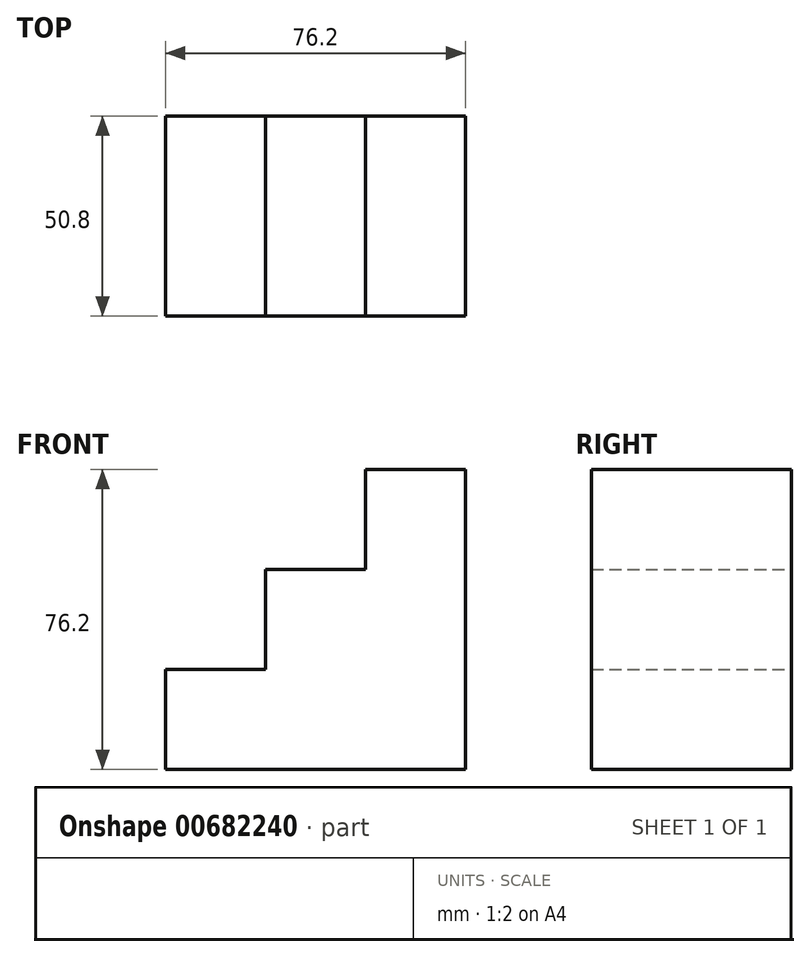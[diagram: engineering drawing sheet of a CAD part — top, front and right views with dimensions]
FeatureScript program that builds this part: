
annotation { "Feature Type Name" : "Feature", "Feature Type Description" : "" }
export const myFeature = defineFeature(function(context is Context, id is Id, definition is map)
    precondition{}
    {
        {
            var Q0;
            Q0=qCreatedBy(makeId("Front.planeOp"),FACE);
            var sketch = newSketch(context, id + "F0", { "sketchPlane" : qUnion([Q0])});
            skLineSegment(sketch, "E0", {"start": v(-41.97, -41.18) * mm, "end": v(34.23, -41.18) * mm});
            skLineSegment(sketch, "E1", {"start": v(34.23, -41.18) * mm, "end": v(34.23, 35.02) * mm});
            skLineSegment(sketch, "E2", {"start": v(34.23, 35.02) * mm, "end": v(8.83, 35.02) * mm});
            skLineSegment(sketch, "E3", {"start": v(8.83, 35.02) * mm, "end": v(8.83, 9.62) * mm});
            skLineSegment(sketch, "E4", {"start": v(8.83, 9.62) * mm, "end": v(-16.57, 9.62) * mm});
            skLineSegment(sketch, "E5", {"start": v(-16.57, 9.62) * mm, "end": v(-16.57, -15.78) * mm});
            skLineSegment(sketch, "E6", {"start": v(-16.57, -15.78) * mm, "end": v(-41.97, -15.78) * mm});
            skLineSegment(sketch, "E7", {"start": v(-41.97, -15.78) * mm, "end": v(-41.97, -41.18) * mm});
            skSolve(sketch);
        }
        {
            var Q0;
            Q0=makeQuery(id+"F0.imprint","IMPRINT",FACE,{"disambiguationData":[TD([[makeQuery(id+"F0.imprint","IMPRINT",EDGE,{"derivedFrom":sQuery(id+"F0.wireOp",EDGE,"E0")}),1.0]])]});
            extrude(context, id + "F1", {"entities" : qUnion([Q0]), "depth" : 50.8 * mm, "offsetDistance" : 25.4 * mm});
        }
    });
